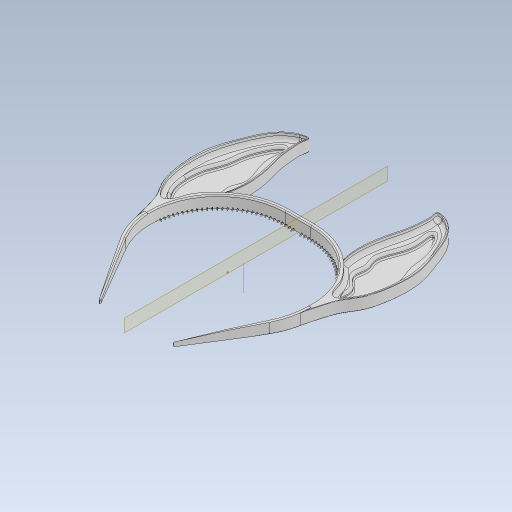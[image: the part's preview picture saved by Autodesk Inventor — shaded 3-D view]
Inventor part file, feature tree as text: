
AUTODESK INVENTOR PART (.ipt)
format: ipt  version: 2023 (Build 270158030, 158C)  size: 2,664,960 bytes
history: native  units: in
note: dims shown in document units (in); Inventor stores cm internally (conversion verified against a paired STEP export)
features: fillet x19, extrude x12, sketch x11, projected_geometry x6, chamfer x2, other x1, pattern_circular x1, mirror x1
ambient origin geometry x8: Origin, YZ Plane, XZ Plane, XY Plane, X Axis, Y Axis, Z Axis, Center Point
bodies: Solid1 (feature_tree), Solid2 (feature_tree)
feature tree (53):
  extrude  "Extrusion1"  Depth=0.1181in
  extrude  "Extrusion2"  Depth=0.3937in TaperAngle=0.0deg
  fillet  "Fillet2"  Radius=0.0433in
  other  "Work Axis1"
  pattern_circular  "Circular Pattern1"  Count=30  [1 undecoded]
  extrude  "Extrusion4"  Depth=4.3307in
  fillet  "Fillet6"  Radius=25.1969in
  fillet  "Fillet7"  Radius=0.7087in
  fillet  "Fillet8"  Radius=4.3307in
  extrude  "Extrusion10"  TaperAngle=0.0deg  [1 undecoded]
  extrude  "Extrusion11"  Depth=0.0394in
  extrude  "Extrusion12"  Depth=0.3937in TaperAngle=0.0deg
  fillet  "Fillet32"  Radius=0.315in
  fillet  "Fillet33"  Radius=0.0591in
  fillet  "Fillet35"  Radius=0.0591in
  chamfer  "Chamfer2"  Distance=0.3346in
  fillet  "Fillet36"  Radius=2.3495in
  extrude  "Extrusion13"  Depth=2.0826in
  mirror  "Mirror1"
  fillet  "Fillet30"  Radius=1.4138in
  fillet  "Fillet28"  Radius=2.5284in
  fillet  "Fillet19"  Radius=1.4901in
  extrude  "Extrusion5"  Depth=2.5146in
  extrude  "Extrusion7"  Depth=2.7368in
  extrude  "Extrusion6"  Depth=1.4623in
  fillet  "Fillet20"  Radius=0.488in
  fillet  "Fillet21"  Radius=0.3104in
  fillet  "Fillet22"  Radius=0.2859in
  fillet  "Fillet23"  Radius=0.2088in
  fillet  "Fillet24"  Radius=0.2171in
  fillet  "Fillet25"  Radius=0.23in
  fillet  "Fillet26"  Radius=0.2362in
  extrude  "Extrusion8"  Depth=0.0787in
  fillet  "Fillet27"  Radius=0.0787in
  extrude  "Extrusion9"  Depth=0.0394in
  chamfer  "Chamfer1"  Distance=0.0394in
  sketch  "Sketch1"  dims[d23=2.2638in d25=0.1181in]
  sketch  "Sketch2"  dims[d27=0.1181in d30=0.3937in d31=0.0in d48=0.0433in d49=0.0in]
  sketch  "Sketch7"  dims[d50=0.0118in]
  sketch  "Sketch8"  dims[d57=0.0787in d58=0.0157in d61=11.811in d62=-0.6184in]
  sketch  "Sketch9"  dims[d65=3.1496in d76=4.3307in d77=25.1969in d78=0.7087in d79=4.3307in]
  sketch  "Sketch11"  dims[d80=0.3937in d81=0.0in d82=0.0in]
  sketch  "Sketch12"  dims[d86=0.0394in d87=0.0394in]
  projected_geometry  "Projected Loop1"
  sketch  "Sketch13"  dims[d88=0.0236in d104=0.3937in d105=0.0in d107=0.315in d108=0.0in d121=0.0591in d122=0.0591in]
  projected_geometry  "Projected Loop2"
  projected_geometry  "Projected Loop3"
  sketch  "Sketch14"  dims[d123=1.378in d125=0.3346in d126=0.0in d130=2.3495in]
  projected_geometry  "Projected Loop4"
  sketch  "Sketch16"  dims[d131=2.2052in d132=2.0826in d133=1.4138in d134=2.5284in d135=1.4901in]
  projected_geometry  "Projected Loop5"
  sketch  "Sketch18"  dims[d136=2.1896in d137=2.5146in d138=2.7368in d139=1.4623in d140=0.488in d141=0.3104in d142=0.2859in d143=0.2088in d144=0.2171in d145=0.23in d147=0.2362in d148=0.0787in d149=0.0787in d150=0.0394in d153=0.0394in d154=0.1181in d155=0.0787in d156=0.0787in d158=23.622in d159=1.9685in d161=7.8078in d162=2.3622in d163=0.7874in d164=0.9817in d165=0.0in d167=0.0787in d168=0.1969in d169=0.1969in d170=0.1181in d171=0.0197in d172=0.0079in d173=0.0394in d174=0.0197in d175=0.0197in d182=0.0984in d183=0.0394in d184=0.0984in d185=0.0394in d186=0.0591in d187=0.0394in d188=0.0197in d189=0.076in d190=0.0in d191=0.0in d192=0.0079in d193=0.0197in d194=0.0787in d195=45.0deg d196=0.0in d197=0.0in d199=0.3937in d200=0.0in d201=0.3543in d202=0.0in d203=0.315in d205=0.1969in d206=0.0in d207=0.1181in d209=0.0118in d210=0.1181in d212=0.0394in d213=0.015in d214=0.0787in d215=45.0deg d216=0.7874in d217=0.4331in d218=2.3622in d219=0.4331in d220=0.0984in d221=0.3937in d222=0.1181in d223=0.0787in d224=0.1969in d225=0.0in]
  projected_geometry  "Projected Loop6"
note: 2 required parameter values undecoded (feature->parameter linkage not recoverable at this tier; creation-order binding heuristic only, values carry confidence <= 0.55)
